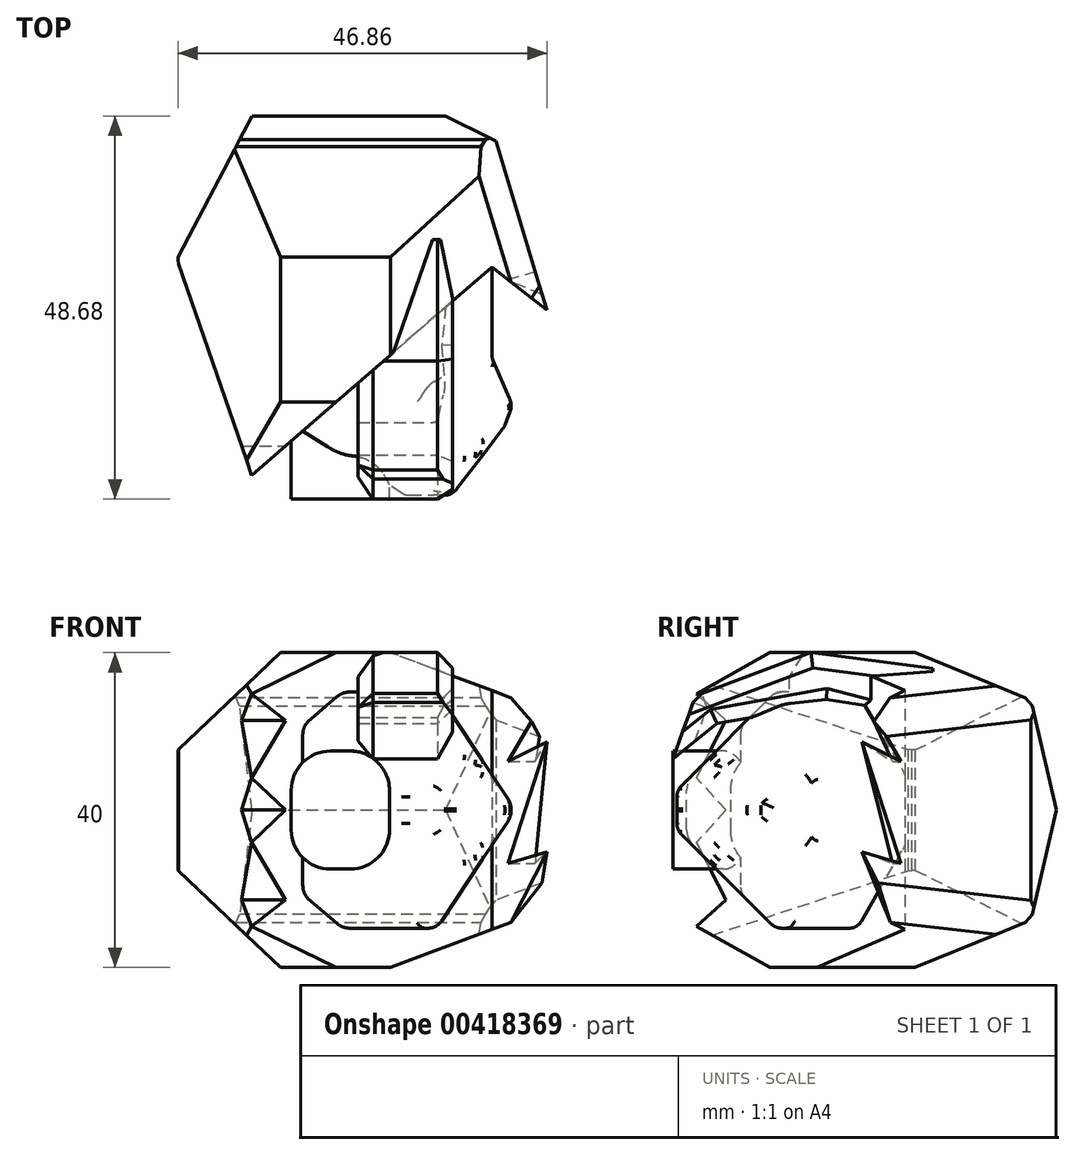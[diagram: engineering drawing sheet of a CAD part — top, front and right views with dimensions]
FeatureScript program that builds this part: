
annotation { "Feature Type Name" : "Feature", "Feature Type Description" : "" }
export const myFeature = defineFeature(function(context is Context, id is Id, definition is map)
    precondition{}
    {
        {
            var Q0;
            Q0=qCreatedBy(makeId("Top.planeOp"),FACE);
            var sketch = newSketch(context, id + "F0", { "sketchPlane" : qUnion([Q0])});
            skLineSegment(sketch, "E0", {"start": v(0, 0) * mm, "end": v(-20, 0) * mm});
            skLineSegment(sketch, "E1", {"start": v(-20, 0) * mm, "end": v(-20, -22.5) * mm});
            skLineSegment(sketch, "E2", {"start": v(-20, -22.5) * mm, "end": v(0, -35) * mm});
            skLineSegment(sketch, "E3", {"start": v(0, 0) * mm, "end": v(7, 0) * mm});
            skLineSegment(sketch, "E4", {"start": v(7, 0) * mm, "end": v(7, -15) * mm});
            skLineSegment(sketch, "E5", {"start": v(7, -15) * mm, "end": v(10, -22) * mm});
            skLineSegment(sketch, "E6", {"start": v(10, -22) * mm, "end": v(0, -35) * mm});
            skSolve(sketch);
        }
        {
            var Q0;
            Q0 = qSketchRegion(id + "F0", true);
            extrude(context, id + "F1", {"entities" : qUnion([Q0]), "depth" : 15 * mm, "hasSecondDirection" : true, "secondDirectionOppositeDirection" : true, "secondDirectionDepth" : 15 * mm});
        }
        {
            var Q0;
            Q0=qCreatedBy(makeId("Front.planeOp"),FACE);
            var sketch = newSketch(context, id + "F2", { "sketchPlane" : qUnion([Q0])});
            skLineSegment(sketch, "E7.0", {"start": v(10, 15) * mm, "end": v(10, -15) * mm, "construction": true});
            skLineSegment(sketch, "E8.0", {"start": v(-20, 15) * mm, "end": v(7, 15) * mm, "construction": true});
            skLineSegment(sketch, "E9", {"start": v(10, 0) * mm, "end": v(0, 15) * mm});
            skLineSegment(sketch, "E10", {"start": v(0, 15) * mm, "end": v(10, 15) * mm});
            skLineSegment(sketch, "E11", {"start": v(10, 0) * mm, "end": v(10, 15) * mm});
            skLineSegment(sketch, "E12.MirrorCS", {"start": v(10, 0) * mm, "end": v(0, -15) * mm});
            skLineSegment(sketch, "E13.MirrorCS", {"start": v(0, -15) * mm, "end": v(10, -15) * mm});
            skLineSegment(sketch, "E14", {"start": v(10, 0) * mm, "end": v(10, -15) * mm});
            skLineSegment(sketch, "E15.0", {"start": v(7, 4.5) * mm, "end": v(7, -4.5) * mm});
            skPoint(sketch, "E16.orphan", {"position": v(7, -15) * mm});
            skSolve(sketch);
        }
        {
            var Q0;
            {var subQ3=sQuery(id+"F2.wireOp",EDGE,"E10");Q0=makeQuery(id+"F2.imprint","IMPRINT",FACE,{"disambiguationData":[TD([[makeQuery(id+"F2.imprint","IMPRINT",EDGE,{"derivedFrom":subQ3}),-1.0]])]});}
            var Q1;
            {var subQ3=sQuery(id+"F2.wireOp",EDGE,"E13.MirrorCS");Q1=makeQuery(id+"F2.imprint","IMPRINT",FACE,{"disambiguationData":[TD([[makeQuery(id+"F2.imprint","IMPRINT",EDGE,{"derivedFrom":subQ3}),1.0]])]});}
            extrude(context, id + "F3", {"entities" : qUnion([Q0, Q1]), "operationType" : NewBodyOperationType.REMOVE, "endBound" : BoundingType.THROUGH_ALL, "depth" : 25 * mm});
        }
        {
            var Q0;
            Q0=qCreatedBy(makeId("Right.planeOp"),FACE);
            var sketch = newSketch(context, id + "F4", { "sketchPlane" : qUnion([Q0])});
            skLineSegment(sketch, "E17.0", {"start": v(-35, 15) * mm, "end": v(0, 15) * mm, "construction": true});
            skLineSegment(sketch, "E18.0", {"start": v(-35, 15) * mm, "end": v(-35, -15) * mm, "construction": true});
            skLineSegment(sketch, "E19", {"start": v(-35, 0) * mm, "end": v(-20, 15) * mm});
            skLineSegment(sketch, "E20", {"start": v(-20, 15) * mm, "end": v(-35, 15) * mm});
            skLineSegment(sketch, "E21", {"start": v(-35, 0) * mm, "end": v(-35, 15) * mm});
            skLineSegment(sketch, "E22", {"start": v(-35, 0) * mm, "end": v(-35, -15) * mm});
            skLineSegment(sketch, "E23.MirrorCS", {"start": v(-35, 0) * mm, "end": v(-20, -15) * mm});
            skLineSegment(sketch, "E24", {"start": v(-20, -15) * mm, "end": v(-35, -15) * mm});
            skLineSegment(sketch, "E25", {"start": v(-32.5, 2.5) * mm, "end": v(-32.5, -2.5) * mm});
            skSolve(sketch);
        }
        {
            var Q0;
            Q0 = qSketchRegion(id + "F4", true);
            extrude(context, id + "F5", {"entities" : qUnion([Q0]), "operationType" : NewBodyOperationType.REMOVE, "endBound" : BoundingType.THROUGH_ALL, "oppositeDirection" : true, "depth" : 25 * mm, "hasSecondDirection" : true, "secondDirectionBound" : SecondDirectionBoundingType.THROUGH_ALL, "secondDirectionOppositeDirection" : false, "secondDirectionDepth" : 25 * mm});
        }
        {
            var Q0;
            Q0=makeQuery(id+"F3.boolean.opBoolean","INTERSECT",EDGE,{"derivedFrom":[makeQuery(id+"F1.opExtrude","SWEPT_FACE",FACE,{"disambiguationData":[OSD([sQuery(id+"F0.wireOp",EDGE,"E6")])]}),makeQuery(id+"F3.opExtrude","SWEPT_FACE",FACE,{"disambiguationData":[OSD([sQuery(id+"F2.wireOp",EDGE,"E9")])]})]});
            var Q1;
            Q1=makeQuery(id+"F3.boolean.opBoolean","INTERSECT",EDGE,{"derivedFrom":[makeQuery(id+"F1.opExtrude","SWEPT_FACE",FACE,{"disambiguationData":[OSD([sQuery(id+"F0.wireOp",EDGE,"E6")])]}),makeQuery(id+"F3.opExtrude","SWEPT_FACE",FACE,{"disambiguationData":[OSD([sQuery(id+"F2.wireOp",EDGE,"E12.MirrorCS")])]})]});
            chamfer(context, id + "F6", {"entities" : qUnion([Q0, Q1]), "width" : 3 * mm, "tangentPropagation" : true});
        }
        {
            var Q0;
            Q0=makeQuery(id+"F5.boolean.opBoolean","INTERSECT",EDGE,{"derivedFrom":[makeQuery(id+"F3.boolean.opBoolean","COPY",FACE,{"derivedFrom":makeQuery(id+"F3.opExtrude","SWEPT_FACE",FACE,{"disambiguationData":[OSD([sQuery(id+"F2.wireOp",EDGE,"E9")])]})}),makeQuery(id+"F5.opExtrude","SWEPT_FACE",FACE,{"disambiguationData":[OSD([sQuery(id+"F4.wireOp",EDGE,"E19")])]})]});
            var Q1;
            Q1=makeQuery(id+"F5.boolean.opBoolean","INTERSECT",EDGE,{"derivedFrom":[makeQuery(id+"F3.boolean.opBoolean","COPY",FACE,{"derivedFrom":makeQuery(id+"F3.opExtrude","SWEPT_FACE",FACE,{"disambiguationData":[OSD([sQuery(id+"F2.wireOp",EDGE,"E12.MirrorCS")])]})}),makeQuery(id+"F5.opExtrude","SWEPT_FACE",FACE,{"disambiguationData":[OSD([sQuery(id+"F4.wireOp",EDGE,"E23.MirrorCS")])]})]});
            var Q2;
            Q2=makeQuery(id+"F5.boolean.opBoolean","INTERSECT",EDGE,{"derivedFrom":[makeQuery(id+"F1.opExtrude","SWEPT_FACE",FACE,{"disambiguationData":[OSD([sQuery(id+"F0.wireOp",EDGE,"E6")])]}),makeQuery(id+"F5.opExtrude","SWEPT_FACE",FACE,{"disambiguationData":[OSD([sQuery(id+"F4.wireOp",EDGE,"E19")])]})]});
            var Q3;
            Q3=makeQuery(id+"F5.boolean.opBoolean","INTERSECT",EDGE,{"derivedFrom":[makeQuery(id+"F1.opExtrude","SWEPT_FACE",FACE,{"disambiguationData":[OSD([sQuery(id+"F0.wireOp",EDGE,"E6")])]}),makeQuery(id+"F5.opExtrude","SWEPT_FACE",FACE,{"disambiguationData":[OSD([sQuery(id+"F4.wireOp",EDGE,"E23.MirrorCS")])]})]});
            chamfer(context, id + "F7", {"entities" : qUnion([Q0, Q1, Q2, Q3]), "width" : 3 * mm, "tangentPropagation" : true});
        }
        {
            var Q0;
            Q0=makeQuery(id+"F3.boolean.opBoolean","COPY",FACE,{"derivedFrom":makeQuery(id+"F3.opExtrude","SWEPT_FACE",FACE,{"disambiguationData":[OSD([sQuery(id+"F2.wireOp",EDGE,"E9")])]})});
            var Q1;
            Q1=makeQuery(id+"F1.opExtrude","SWEPT_FACE",FACE,{"disambiguationData":[OSD([sQuery(id+"F0.wireOp",EDGE,"E4")])]});
            var Q2;
            Q2=makeQuery(id+"F3.boolean.opBoolean","COPY",FACE,{"derivedFrom":makeQuery(id+"F3.opExtrude","SWEPT_FACE",FACE,{"disambiguationData":[OSD([sQuery(id+"F2.wireOp",EDGE,"E12.MirrorCS")])]})});
            var Q3;
            Q3=makeQuery(id+"F1.opExtrude","SWEPT_FACE",FACE,{"disambiguationData":[OSD([sQuery(id+"F0.wireOp",EDGE,"E5")])]});
            var Q4;
            Q4=makeQuery(id+"F6.opChamfer","BLEND_FACE",FACE,{"disambiguationData":[OSD([sQuery(id+"F0.wireOp",EDGE,"E6"),sQuery(id+"F2.wireOp",EDGE,"E12.MirrorCS")])]});
            var Q5;
            Q5=makeQuery(id+"F6.opChamfer","BLEND_FACE",FACE,{"disambiguationData":[OSD([sQuery(id+"F0.wireOp",EDGE,"E6"),sQuery(id+"F2.wireOp",EDGE,"E9")])]});
            var Q6;
            Q6=makeQuery(id+"F1.opExtrude","SWEPT_FACE",FACE,{"disambiguationData":[OSD([sQuery(id+"F0.wireOp",EDGE,"E6")])]});
            var Q7;
            Q7=makeQuery(id+"F7.opChamfer","BLEND_FACE",FACE,{"disambiguationData":[OSD([sQuery(id+"F0.wireOp",EDGE,"E6"),sQuery(id+"F4.wireOp",EDGE,"E23.MirrorCS")])]});
            var Q8;
            Q8=makeQuery(id+"F7.opChamfer","BLEND_FACE",FACE,{"disambiguationData":[OSD([sQuery(id+"F0.wireOp",EDGE,"E6"),sQuery(id+"F4.wireOp",EDGE,"E19")])]});
            var Q9;
            Q9=makeQuery(id+"F7.opChamfer","BLEND_FACE",FACE,{"disambiguationData":[OSD([sQuery(id+"F2.wireOp",EDGE,"E9"),sQuery(id+"F4.wireOp",EDGE,"E19")])]});
            var Q10;
            {var subQ0=makeQuery(id+"F5.opExtrude","SWEPT_FACE",FACE,{"disambiguationData":[OSD([sQuery(id+"F4.wireOp",EDGE,"E23.MirrorCS")])]});Q10=makeQuery(id+"F7.opChamfer","BLEND_EDGE",EDGE,{"blendedFrom":[makeQuery(id+"F5.boolean.opBoolean","INTERSECT",EDGE,{"derivedFrom":[makeQuery(id+"F3.boolean.opBoolean","COPY",FACE,{"derivedFrom":makeQuery(id+"F3.opExtrude","SWEPT_FACE",FACE,{"disambiguationData":[OSD([sQuery(id+"F2.wireOp",EDGE,"E12.MirrorCS")])]})}),subQ0]}),makeQuery(id+"F5.boolean.opBoolean","COPY",FACE,{"derivedFrom":subQ0})],"blendedInto":[makeQuery(id+"F5.boolean.opBoolean","COPY",FACE,{"derivedFrom":subQ0})]});}
            var Q11;
            Q11=makeQuery(id+"F5.boolean.opBoolean","COPY",FACE,{"derivedFrom":makeQuery(id+"F5.opExtrude","SWEPT_FACE",FACE,{"disambiguationData":[OSD([sQuery(id+"F4.wireOp",EDGE,"E19")])]})});
            var Q12;
            Q12=makeQuery(id+"F5.boolean.opBoolean","COPY",FACE,{"derivedFrom":makeQuery(id+"F5.opExtrude","SWEPT_FACE",FACE,{"disambiguationData":[OSD([sQuery(id+"F4.wireOp",EDGE,"E23.MirrorCS")])]})});
            var Q13;
            Q13=makeQuery(id+"F1.opExtrude","SWEPT_FACE",FACE,{"disambiguationData":[OSD([sQuery(id+"F0.wireOp",EDGE,"E2")])]});
            fillet(context, id + "F8", {"entities" : qUnion([Q0, Q1, Q2, Q3, Q4, Q5, Q6, Q7, Q8, Q9, Q10, Q11, Q12, Q13]), "radius" : 2 * mm, "tangentPropagation" : true, "allowEdgeOverflow" : false});
        }
        {
            var Q0;
            Q0=qCreatedBy(makeId("Top.planeOp"),FACE);
            var sketch = newSketch(context, id + "F9", { "sketchPlane" : qUnion([Q0])});
            skLineSegment(sketch, "E26", {"start": v(-6, -18) * mm, "end": v(-18.5, -18) * mm});
            skLineSegment(sketch, "E27", {"start": v(-18.5, -18) * mm, "end": v(-18.5, -33) * mm});
            skLineSegment(sketch, "E28", {"start": v(-18.5, -33) * mm, "end": v(-6, -33) * mm});
            skLineSegment(sketch, "E29", {"start": v(-6, -33) * mm, "end": v(-6, -18) * mm});
            skSolve(sketch);
        }
        {
            var Q0;
            Q0 = qSketchRegion(id + "F9", true);
            extrude(context, id + "F10", {"entities" : qUnion([Q0]), "operationType" : NewBodyOperationType.ADD, "depth" : 7.5 * mm, "hasSecondDirection" : true, "secondDirectionOppositeDirection" : true, "secondDirectionDepth" : 7.5 * mm});
        }
        {
            var Q0;
            Q0=makeQuery(id+"F10.opExtrude","CAP_EDGE",EDGE,{"disambiguationData":[OSD([sQuery(id+"F9.wireOp",EDGE,"E27")])],"isStart":false});
            var Q1;
            Q1=makeQuery(id+"F10.opExtrude","CAP_EDGE",EDGE,{"disambiguationData":[OSD([sQuery(id+"F9.wireOp",EDGE,"E27")])],"isStart":true});
            var Q2;
            Q2=makeQuery(id+"F10.opExtrude","CAP_EDGE",EDGE,{"disambiguationData":[OSD([sQuery(id+"F9.wireOp",EDGE,"E29")])],"isStart":false});
            var Q3;
            Q3=makeQuery(id+"F10.opExtrude","CAP_EDGE",EDGE,{"disambiguationData":[OSD([sQuery(id+"F9.wireOp",EDGE,"E29")])],"isStart":true});
            fillet(context, id + "F11", {"entities" : qUnion([Q0, Q1, Q2, Q3]), "radius" : 5 * mm, "tangentPropagation" : true, "allowEdgeOverflow" : false});
        }
        {
            var Q0;
            Q0=qCreatedBy(makeId("Top.planeOp"),FACE);
            var sketch = newSketch(context, id + "F12", { "sketchPlane" : qUnion([Q0])});
            skLineSegment(sketch, "E30", {"start": v(-2.5, 17.5) * mm, "end": v(7.5, 12.5) * mm});
            skLineSegment(sketch, "E31", {"start": v(7.5, 12.5) * mm, "end": v(14, -9) * mm});
            skLineSegment(sketch, "E32", {"start": v(14, -9) * mm, "end": v(7, -3.5) * mm});
            skLineSegment(sketch, "E33.0", {"start": v(7, -2) * mm, "end": v(7, -14.59) * mm, "construction": true});
            skLineSegment(sketch, "E34", {"start": v(-2.5, 17.5) * mm, "end": v(-22.5, 17.5) * mm});
            skLineSegment(sketch, "E35", {"start": v(-22.5, 17.5) * mm, "end": v(-33, -2.5) * mm});
            skLineSegment(sketch, "E36", {"start": v(-33, -2.5) * mm, "end": v(-23.5, -30) * mm});
            skLineSegment(sketch, "E37", {"start": v(-23.5, -30) * mm, "end": v(7, -3.5) * mm});
            skSolve(sketch);
        }
        {
            var Q0;
            Q0 = qSketchRegion(id + "F12", true);
            extrude(context, id + "F13", {"entities" : qUnion([Q0]), "operationType" : NewBodyOperationType.ADD, "depth" : 20 * mm, "hasSecondDirection" : true, "secondDirectionOppositeDirection" : true, "secondDirectionDepth" : 20 * mm});
        }
        {
            var Q0;
            Q0=makeQuery(id+"F13.opExtrude","SWEPT_FACE",FACE,{"disambiguationData":[OSD([sQuery(id+"F12.wireOp",EDGE,"E31")])]});
            var sketch = newSketch(context, id + "F14", { "sketchPlane" : qUnion([Q0])});
            skSolve(sketch);
        }
        {
            var Q0;
            {var subQ0=sQuery(id+"F12.wireOp",EDGE,"E31");Q0=makeQuery(id+"F14.imprint","IMPRINT",FACE,{"disambiguationData":[TD([[makeQuery(id+"F14.imprint","IMPRINT",EDGE,{"derivedFrom":makeQuery(id+"F13.opExtrude","CAP_EDGE",EDGE,{"disambiguationData":[OSD([subQ0])],"isStart":true})}),-1.0]])]});}
            var sketch = newSketch(context, id + "F15", { "sketchPlane" : qUnion([Q0])});
            skLineSegment(sketch, "E38.0", {"start": v(-12.67, 20) * mm, "end": v(-12.67, -20) * mm, "construction": true});
            skLineSegment(sketch, "E39", {"start": v(-12.67, 14.7) * mm, "end": v(-7.5, 6.17) * mm});
            skLineSegment(sketch, "E40", {"start": v(-7.5, 6.17) * mm, "end": v(-12.67, 8.67) * mm});
            skLineSegment(sketch, "E41", {"start": v(-12.67, 8.67) * mm, "end": v(-7.5, -6.76) * mm});
            skLineSegment(sketch, "E42", {"start": v(-7.5, -6.76) * mm, "end": v(-12.67, -5.29) * mm});
            skLineSegment(sketch, "E43", {"start": v(-12.67, -5.29) * mm, "end": v(-7.5, -14.99) * mm});
            skLineSegment(sketch, "E44", {"start": v(-7.5, -14.99) * mm, "end": v(-12.67, -16.01) * mm});
            skLineSegment(sketch, "E45", {"start": v(-12.67, -16.01) * mm, "end": v(-12.67, 14.7) * mm});
            skSolve(sketch);
        }
        {
            var Q0;
            Q0 = qSketchRegion(id + "F15", true);
            extrude(context, id + "F16", {"entities" : qUnion([Q0]), "operationType" : NewBodyOperationType.REMOVE, "oppositeDirection" : true, "depth" : 4 * mm});
        }
        {
            var Q0;
            Q0=qCreatedBy(makeId("Right.planeOp"),FACE);
            var sketch = newSketch(context, id + "F17", { "sketchPlane" : qUnion([Q0])});
            skLineSegment(sketch, "E46.0", {"start": v(12.5, 20) * mm, "end": v(12.5, -20) * mm, "construction": true});
            skLineSegment(sketch, "E47.0", {"start": v(12.5, 20) * mm, "end": v(-9, 20) * mm, "construction": true});
            skLineSegment(sketch, "E48", {"start": v(15.68, 0) * mm, "end": v(12.5, 13.98) * mm});
            skLineSegment(sketch, "E49", {"start": v(12.5, 13.98) * mm, "end": v(-2.23, 20) * mm});
            skPoint(sketch, "E50.0", {"position": v(17.5, 20) * mm});
            skLineSegment(sketch, "E51", {"start": v(17.5, 20) * mm, "end": v(-2.23, 20) * mm});
            skLineSegment(sketch, "E52", {"start": v(17.5, 20) * mm, "end": v(17.5, 0) * mm});
            skLineSegment(sketch, "E53.MirrorCS", {"start": v(17.5, -20) * mm, "end": v(17.5, 0) * mm});
            skLineSegment(sketch, "E54.MirrorCS", {"start": v(17.5, -20) * mm, "end": v(-2.23, -20) * mm});
            skLineSegment(sketch, "E55.MirrorCS", {"start": v(12.5, -13.98) * mm, "end": v(-2.23, -20) * mm});
            skLineSegment(sketch, "E56.MirrorCS", {"start": v(15.68, 0) * mm, "end": v(12.5, -13.98) * mm});
            skSolve(sketch);
        }
        {
            var Q0;
            Q0 = qSketchRegion(id + "F17", true);
            extrude(context, id + "F18", {"entities" : qUnion([Q0]), "operationType" : NewBodyOperationType.REMOVE, "endBound" : BoundingType.THROUGH_ALL, "oppositeDirection" : true, "depth" : 25 * mm, "hasSecondDirection" : true, "secondDirectionBound" : SecondDirectionBoundingType.THROUGH_ALL, "secondDirectionOppositeDirection" : false, "secondDirectionDepth" : 25 * mm});
        }
        {
            var Q0;
            Q0=qCreatedBy(makeId("Front.planeOp"),FACE);
            var sketch = newSketch(context, id + "F19", { "sketchPlane" : qUnion([Q0])});
            skLineSegment(sketch, "E57.0", {"start": v(-33, 20) * mm, "end": v(-33, -20) * mm, "construction": true});
            skLineSegment(sketch, "E58.0", {"start": v(-32.86, 20) * mm, "end": v(11.95, 20) * mm, "construction": true});
            skLineSegment(sketch, "E59", {"start": v(-33, 7.5) * mm, "end": v(-19.86, 20) * mm});
            skLineSegment(sketch, "E60", {"start": v(-19.86, 20) * mm, "end": v(-32.86, 20) * mm});
            skLineSegment(sketch, "E61", {"start": v(-33, 7.5) * mm, "end": v(-32.86, 20) * mm});
            skLineSegment(sketch, "E62", {"start": v(-5.86, 20) * mm, "end": v(14.14, 12.5) * mm});
            skLineSegment(sketch, "E63", {"start": v(14.14, 12.5) * mm, "end": v(14.14, 20) * mm});
            skLineSegment(sketch, "E64", {"start": v(14.14, 20) * mm, "end": v(-5.86, 20) * mm});
            skLineSegment(sketch, "E65.MirrorCS", {"start": v(14.14, -20) * mm, "end": v(-5.86, -20) * mm});
            skLineSegment(sketch, "E66.MirrorCS", {"start": v(-19.86, -20) * mm, "end": v(-32.86, -20) * mm});
            skLineSegment(sketch, "E67.MirrorCS", {"start": v(-33, -7.5) * mm, "end": v(-32.86, -20) * mm});
            skLineSegment(sketch, "E68.MirrorCS", {"start": v(-32.86, -20) * mm, "end": v(11.95, -20) * mm, "construction": true});
            skLineSegment(sketch, "E69.MirrorCS", {"start": v(-33, -7.5) * mm, "end": v(-19.86, -20) * mm});
            skLineSegment(sketch, "E70.MirrorCS", {"start": v(-5.86, -20) * mm, "end": v(14.14, -12.5) * mm});
            skLineSegment(sketch, "E71.MirrorCS", {"start": v(14.14, -12.5) * mm, "end": v(14.14, -20) * mm});
            skLineSegment(sketch, "E72.bottom", {"start": v(-32.86, 20) * mm, "end": v(-35.86, 20) * mm});
            skLineSegment(sketch, "E72.top", {"start": v(-32.86, -20) * mm, "end": v(-35.86, -20) * mm});
            skLineSegment(sketch, "E72.left", {"start": v(-32.86, 20) * mm, "end": v(-32.86, -20) * mm});
            skLineSegment(sketch, "E72.right", {"start": v(-35.86, 20) * mm, "end": v(-35.86, -20) * mm});
            skSolve(sketch);
        }
        {
            var Q0;
            Q0 = qSketchRegion(id + "F19", true);
            extrude(context, id + "F20", {"entities" : qUnion([Q0]), "operationType" : NewBodyOperationType.REMOVE, "endBound" : BoundingType.THROUGH_ALL, "oppositeDirection" : true, "depth" : 25 * mm, "hasSecondDirection" : true, "secondDirectionBound" : SecondDirectionBoundingType.THROUGH_ALL, "secondDirectionOppositeDirection" : false, "secondDirectionDepth" : 25 * mm});
        }
        {
            var Q0;
            Q0=qCreatedBy(makeId("Right.planeOp"),FACE);
            var sketch = newSketch(context, id + "F21", { "sketchPlane" : qUnion([Q0])});
            skLineSegment(sketch, "E73.0", {"start": v(-26.84, 20) * mm, "end": v(-14.67, 20) * mm, "construction": true});
            skLineSegment(sketch, "E74", {"start": v(-20.67, 20) * mm, "end": v(-33.17, 20) * mm});
            skLineSegment(sketch, "E75", {"start": v(-33.17, 20) * mm, "end": v(-33.17, 13) * mm});
            skLineSegment(sketch, "E76", {"start": v(-33.17, 13) * mm, "end": v(-20.67, 20) * mm});
            skLineSegment(sketch, "E77.MirrorCS", {"start": v(-33.17, -20) * mm, "end": v(-33.17, -13) * mm});
            skLineSegment(sketch, "E78.MirrorCS", {"start": v(-26.84, -20) * mm, "end": v(-14.67, -20) * mm, "construction": true});
            skLineSegment(sketch, "E79.MirrorCS", {"start": v(-20.67, -20) * mm, "end": v(-33.17, -20) * mm});
            skLineSegment(sketch, "E80.MirrorCS", {"start": v(-33.17, -13) * mm, "end": v(-20.67, -20) * mm});
            skSolve(sketch);
        }
        {
            var Q0;
            Q0 = qSketchRegion(id + "F21", true);
            extrude(context, id + "F22", {"entities" : qUnion([Q0]), "operationType" : NewBodyOperationType.REMOVE, "oppositeDirection" : true, "depth" : 25 * mm});
        }
        {
            var Q0;
            Q0=qCreatedBy(makeId("Right.planeOp"),FACE);
            cPlane(context, id + "F23", {"entities" : qUnion([Q0]), "cplaneType" : CPlaneType.OFFSET, "offset" : 19 * mm, "oppositeDirection" : true, "width" : 150 * mm, "height" : 150 * mm});
        }
        {
            var Q0;
            Q0=qCreatedBy(id+"F23.planeOp",FACE);
            var sketch = newSketch(context, id + "F24", { "sketchPlane" : qUnion([Q0])});
            skLineSegment(sketch, "E81.0", {"start": v(-30, 14.78) * mm, "end": v(-30, -14.78) * mm, "construction": true});
            skLineSegment(sketch, "E82", {"start": v(-30, -14.78) * mm, "end": v(-26.26, -11.41) * mm});
            skLineSegment(sketch, "E83", {"start": v(-26.26, -11.41) * mm, "end": v(-30, -4.12) * mm});
            skLineSegment(sketch, "E84", {"start": v(-30, -4.12) * mm, "end": v(-26.26, 0) * mm});
            skLineSegment(sketch, "E85.MirrorCS", {"start": v(-30, 4.12) * mm, "end": v(-26.26, 0) * mm});
            skLineSegment(sketch, "E86.MirrorCS", {"start": v(-26.26, 11.41) * mm, "end": v(-30, 4.12) * mm});
            skLineSegment(sketch, "E87.MirrorCS", {"start": v(-30, 14.78) * mm, "end": v(-26.26, 11.41) * mm});
            skLineSegment(sketch, "E88", {"start": v(-30, -14.78) * mm, "end": v(-30, 14.78) * mm});
            skSolve(sketch);
        }
        {
            var Q0;
            Q0 = qSketchRegion(id + "F24", true);
            extrude(context, id + "F25", {"entities" : qUnion([Q0]), "operationType" : NewBodyOperationType.REMOVE, "oppositeDirection" : true, "depth" : 10 * mm});
        }
        {
            var Q0;
            Q0=makeQuery(id+"F20.boolean.opBoolean","INTERSECT",EDGE,{"derivedFrom":[makeQuery(id+"F13.opExtrude","SWEPT_FACE",FACE,{"disambiguationData":[OSD([sQuery(id+"F12.wireOp",EDGE,"E31")])]}),makeQuery(id+"F20.opExtrude","SWEPT_FACE",FACE,{"disambiguationData":[OSD([sQuery(id+"F19.wireOp",EDGE,"E62")])]})]});
            var Q1;
            Q1=makeQuery(id+"F20.boolean.opBoolean","INTERSECT",EDGE,{"derivedFrom":[makeQuery(id+"F13.opExtrude","SWEPT_FACE",FACE,{"disambiguationData":[OSD([sQuery(id+"F12.wireOp",EDGE,"E31")])]}),makeQuery(id+"F20.opExtrude","SWEPT_FACE",FACE,{"disambiguationData":[OSD([sQuery(id+"F19.wireOp",EDGE,"E70.MirrorCS")])]})]});
            chamfer(context, id + "F26", {"entities" : qUnion([Q0, Q1]), "width" : 5 * mm, "tangentPropagation" : true});
        }
        {
            var Q0;
            Q0=makeQuery(id+"F20.boolean.opBoolean","INTERSECT",EDGE,{"derivedFrom":[makeQuery(id+"F13.opExtrude","SWEPT_FACE",FACE,{"disambiguationData":[OSD([sQuery(id+"F12.wireOp",EDGE,"E36")])]}),makeQuery(id+"F20.opExtrude","SWEPT_FACE",FACE,{"disambiguationData":[OSD([sQuery(id+"F19.wireOp",EDGE,"E72.left")])]})]});
            var Q1;
            Q1=makeQuery(id+"F22.boolean.opBoolean","COPY",EDGE,{"derivedFrom":makeQuery(id+"F22.opExtrude","SWEPT_EDGE",EDGE,{"disambiguationData":[OSD([sQuery(id+"F21.wireOp",EDGE,"E74"),sQuery(id+"F21.wireOp",EDGE,"E76")])]})});
            var Q2;
            Q2=makeQuery(id+"F22.boolean.opBoolean","COPY",EDGE,{"derivedFrom":makeQuery(id+"F22.opExtrude","SWEPT_EDGE",EDGE,{"disambiguationData":[OSD([sQuery(id+"F21.wireOp",EDGE,"E79.MirrorCS"),sQuery(id+"F21.wireOp",EDGE,"E80.MirrorCS")])]})});
            var Q3;
            Q3=makeQuery(id+"F18.boolean.opBoolean","COPY",EDGE,{"derivedFrom":makeQuery(id+"F18.opExtrude","SWEPT_EDGE",EDGE,{"disambiguationData":[OSD([sQuery(id+"F17.wireOp",EDGE,"E48"),sQuery(id+"F17.wireOp",EDGE,"E49")])]})});
            var Q4;
            Q4=makeQuery(id+"F18.boolean.opBoolean","COPY",EDGE,{"derivedFrom":makeQuery(id+"F18.opExtrude","SWEPT_EDGE",EDGE,{"disambiguationData":[OSD([sQuery(id+"F17.wireOp",EDGE,"E55.MirrorCS"),sQuery(id+"F17.wireOp",EDGE,"E56.MirrorCS")])]})});
            chamfer(context, id + "F27", {"entities" : qUnion([Q0, Q1, Q2, Q3, Q4]), "width" : 1.5 * mm, "tangentPropagation" : true});
        }
        {
            var Q0;
            Q0=qCreatedBy(makeId("Right.planeOp"),FACE);
            var sketch = newSketch(context, id + "F28", { "sketchPlane" : qUnion([Q0])});
            skLineSegment(sketch, "E89", {"start": v(0, 10) * mm, "end": v(-13.5, 13.5) * mm});
            skLineSegment(sketch, "E90", {"start": v(-13.5, 13.5) * mm, "end": v(-27.4, 11) * mm});
            skLineSegment(sketch, "E91", {"start": v(-27.4, 11) * mm, "end": v(-33, 6.52) * mm});
            skLineSegment(sketch, "E92", {"start": v(-33, 6.52) * mm, "end": v(-30.14, 14.52) * mm});
            skLineSegment(sketch, "E93", {"start": v(-30.14, 14.52) * mm, "end": v(-15.45, 20) * mm});
            skLineSegment(sketch, "E94", {"start": v(-15.45, 20) * mm, "end": v(0, 18) * mm});
            skLineSegment(sketch, "E95", {"start": v(0, 18) * mm, "end": v(0, 10) * mm});
            skSolve(sketch);
        }
        {
            var Q0;
            Q0 = qSketchRegion(id + "F28", true);
            extrude(context, id + "F29", {"entities" : qUnion([Q0]), "operationType" : NewBodyOperationType.ADD, "oppositeDirection" : true, "depth" : 10 * mm, "hasSecondDirection" : true, "secondDirectionOppositeDirection" : false, "secondDirectionDepth" : 2 * mm});
        }
        {
            var Q0;
            Q0=makeQuery(id+"F29.opExtrude","CAP_EDGE",EDGE,{"disambiguationData":[OSD([sQuery(id+"F28.wireOp",EDGE,"E94")])],"isStart":true});
            var Q1;
            Q1=makeQuery(id+"F29.opExtrude","CAP_EDGE",EDGE,{"disambiguationData":[OSD([sQuery(id+"F28.wireOp",EDGE,"E93")])],"isStart":true});
            var Q2;
            Q2=makeQuery(id+"F29.opExtrude","CAP_EDGE",EDGE,{"disambiguationData":[OSD([sQuery(id+"F28.wireOp",EDGE,"E89")])],"isStart":true});
            var Q3;
            Q3=makeQuery(id+"F29.opExtrude","CAP_EDGE",EDGE,{"disambiguationData":[OSD([sQuery(id+"F28.wireOp",EDGE,"E90")])],"isStart":true});
            var Q4;
            Q4=makeQuery(id+"F29.opExtrude","CAP_EDGE",EDGE,{"disambiguationData":[OSD([sQuery(id+"F28.wireOp",EDGE,"E91")])],"isStart":true});
            var Q5;
            Q5=makeQuery(id+"F29.opExtrude","CAP_EDGE",EDGE,{"disambiguationData":[OSD([sQuery(id+"F28.wireOp",EDGE,"E93")])],"isStart":false});
            var Q6;
            Q6=makeQuery(id+"F29.opExtrude","SWEPT_EDGE",EDGE,{"disambiguationData":[OSD([sQuery(id+"F28.wireOp",EDGE,"E92"),sQuery(id+"F28.wireOp",EDGE,"E93")])]});
            var Q7;
            Q7=makeQuery(id+"F29.opExtrude","CAP_EDGE",EDGE,{"disambiguationData":[OSD([sQuery(id+"F28.wireOp",EDGE,"E92")])],"isStart":false});
            chamfer(context, id + "F30", {"entities" : qUnion([Q0, Q1, Q2, Q3, Q4, Q5, Q6, Q7]), "width" : 1.9 * mm, "tangentPropagation" : true});
        }
    });
